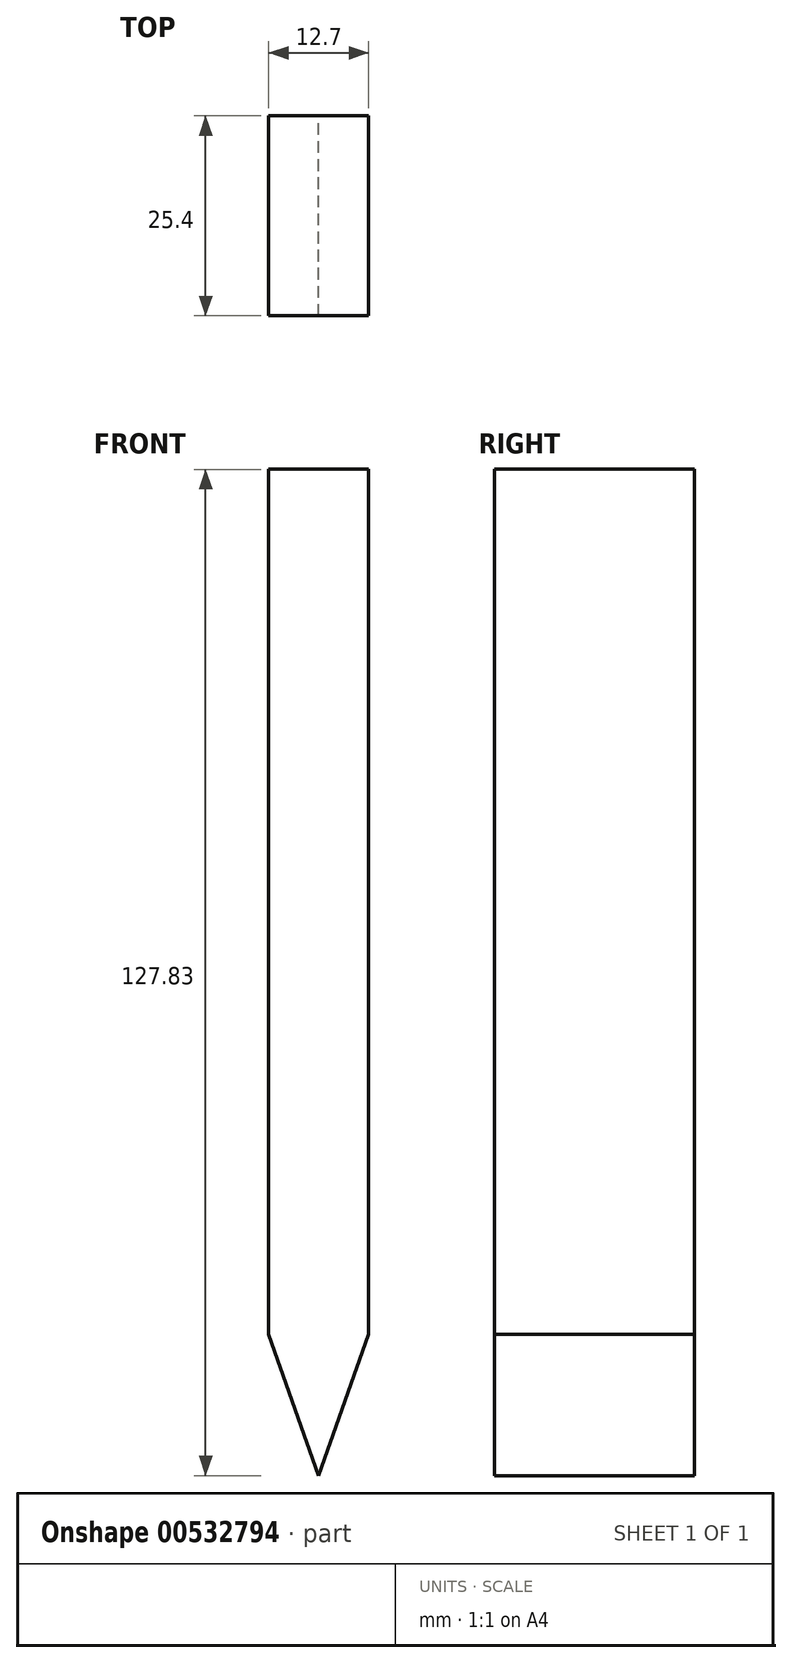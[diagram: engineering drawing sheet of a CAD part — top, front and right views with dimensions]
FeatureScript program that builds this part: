
annotation { "Feature Type Name" : "Feature", "Feature Type Description" : "" }
export const myFeature = defineFeature(function(context is Context, id is Id, definition is map)
    precondition{}
    {
        {
            var Q0;
            Q0=qCreatedBy(makeId("Front.planeOp"),FACE);
            var sketch = newSketch(context, id + "F0", { "sketchPlane" : qUnion([Q0])});
            skLineSegment(sketch, "E0", {"start": v(-50.76, 60.34) * mm, "end": v(-50.76, -41.26) * mm});
            skLineSegment(sketch, "E1", {"start": v(-50.76, 60.34) * mm, "end": v(-38.06, 60.34) * mm});
            skLineSegment(sketch, "E2", {"start": v(-38.06, 60.34) * mm, "end": v(-38.06, -41.26) * mm});
            skLineSegment(sketch, "E3", {"start": v(-50.76, -41.26) * mm, "end": v(-38.06, -41.26) * mm});
            skLineSegment(sketch, "E4", {"start": v(-50.76, -41.26) * mm, "end": v(-44.41, -59.22) * mm});
            skLineSegment(sketch, "E5", {"start": v(-44.41, -59.22) * mm, "end": v(-38.06, -41.26) * mm});
            skLineSegment(sketch, "E6", {"start": v(-50.76, 60.34) * mm, "end": v(-50.76, 68.61) * mm});
            skLineSegment(sketch, "E7", {"start": v(-38.06, 60.34) * mm, "end": v(-38.06, 68.61) * mm});
            skLineSegment(sketch, "E8", {"start": v(-50.76, 68.61) * mm, "end": v(-38.06, 68.61) * mm});
            skSolve(sketch);
        }
        {
            var Q0;
            Q0=makeQuery(id+"F0.imprint","IMPRINT",FACE,{"disambiguationData":[TD([[makeQuery(id+"F0.imprint","IMPRINT",EDGE,{"derivedFrom":sQuery(id+"F0.wireOp",EDGE,"E0")}),1.0]])]});
            var Q1;
            Q1=makeQuery(id+"F0.imprint","IMPRINT",FACE,{"disambiguationData":[TD([[makeQuery(id+"F0.imprint","IMPRINT",EDGE,{"derivedFrom":sQuery(id+"F0.wireOp",EDGE,"E1")}),1.0]])]});
            var Q2;
            Q2=makeQuery(id+"F0.imprint","IMPRINT",FACE,{"disambiguationData":[TD([[makeQuery(id+"F0.imprint","IMPRINT",EDGE,{"derivedFrom":sQuery(id+"F0.wireOp",EDGE,"E3")}),-1.0]])]});
            extrude(context, id + "F1", {"entities" : qUnion([Q0, Q1, Q2]), "depth" : 25.4 * mm, "offsetDistance" : 25.4 * mm});
        }
    });
